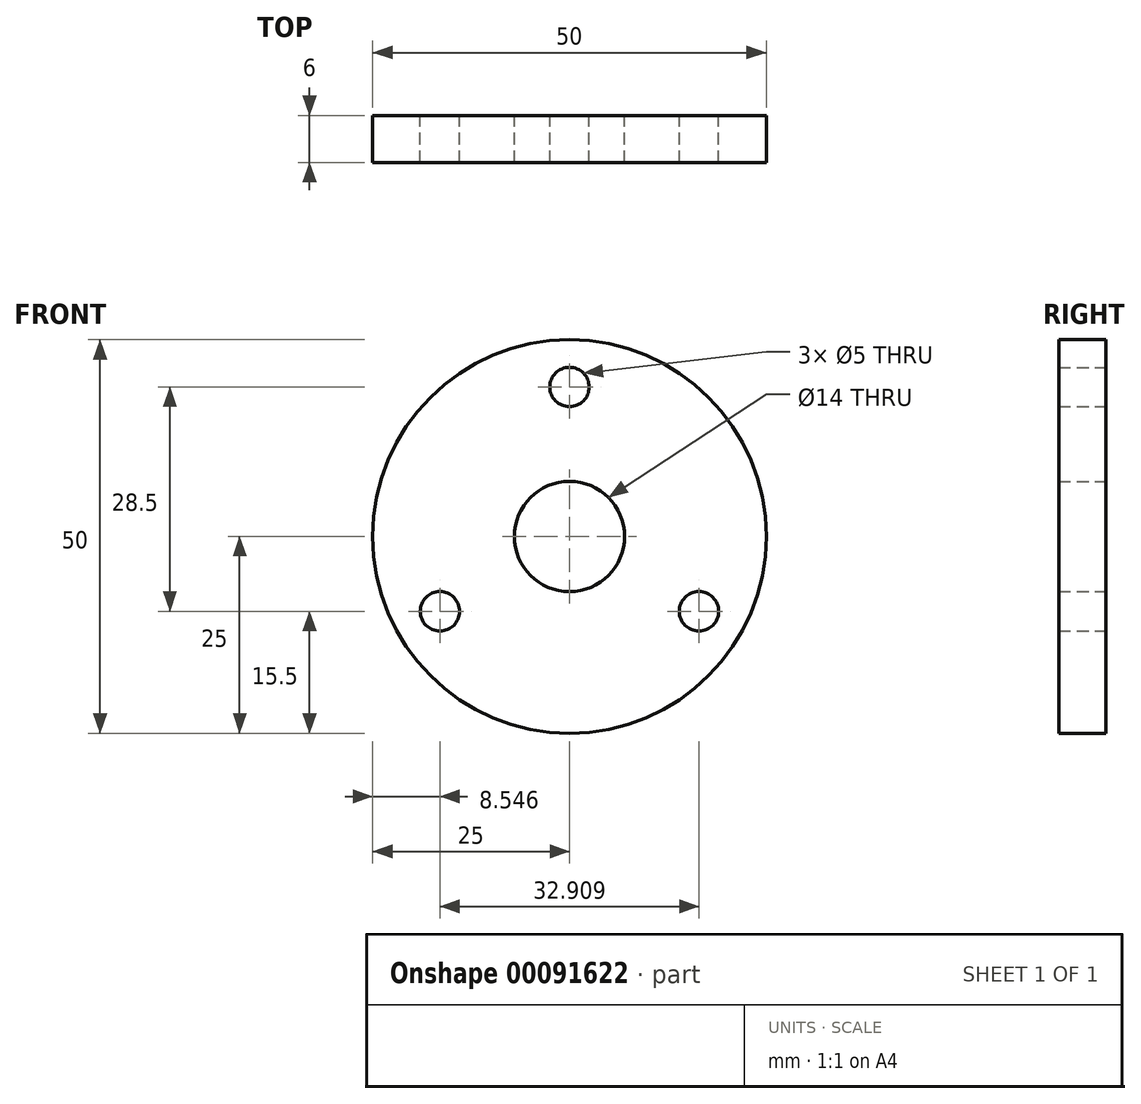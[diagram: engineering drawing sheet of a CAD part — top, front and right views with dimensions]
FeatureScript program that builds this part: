
annotation { "Feature Type Name" : "Feature", "Feature Type Description" : "" }
export const myFeature = defineFeature(function(context is Context, id is Id, definition is map)
    precondition{}
    {
        {
            var Q0;
            Q0=qCreatedBy(makeId("Front.planeOp"),FACE);
            var sketch = newSketch(context, id + "F0", { "sketchPlane" : qUnion([Q0])});
            skCircle(sketch, "E0", {"center": v(0, 0) * mm, "radius": 25 * mm});
            skCircle(sketch, "E1", {"center": v(0, 0) * mm, "radius": 7 * mm});
            skCircle(sketch, "E2", {"center": v(0, 19) * mm, "radius": 2.5 * mm});
            skCircle(sketch, "E3.1.0", {"center": v(-16.45, -9.5) * mm, "radius": 2.5 * mm});
            skCircle(sketch, "E3.2.0", {"center": v(16.45, -9.5) * mm, "radius": 2.5 * mm});
            skLineSegment(sketch, "E4", {"start": v(-16.45, -9.5) * mm, "end": v(0, 0) * mm, "construction": true});
            skLineSegment(sketch, "E5", {"start": v(0, 0) * mm, "end": v(16.45, -9.5) * mm, "construction": true});
            skSolve(sketch);
        }
        {
            var Q0;
            Q0=makeQuery(id+"F0.imprint","IMPRINT",FACE,{"disambiguationData":[TD([[makeQuery(id+"F0.imprint","IMPRINT",EDGE,{"derivedFrom":sQuery(id+"F0.wireOp",EDGE,"E0")}),1.0]])]});
            extrude(context, id + "F1", {"entities" : qUnion([Q0]), "depth" : 6 * mm});
        }
    });
